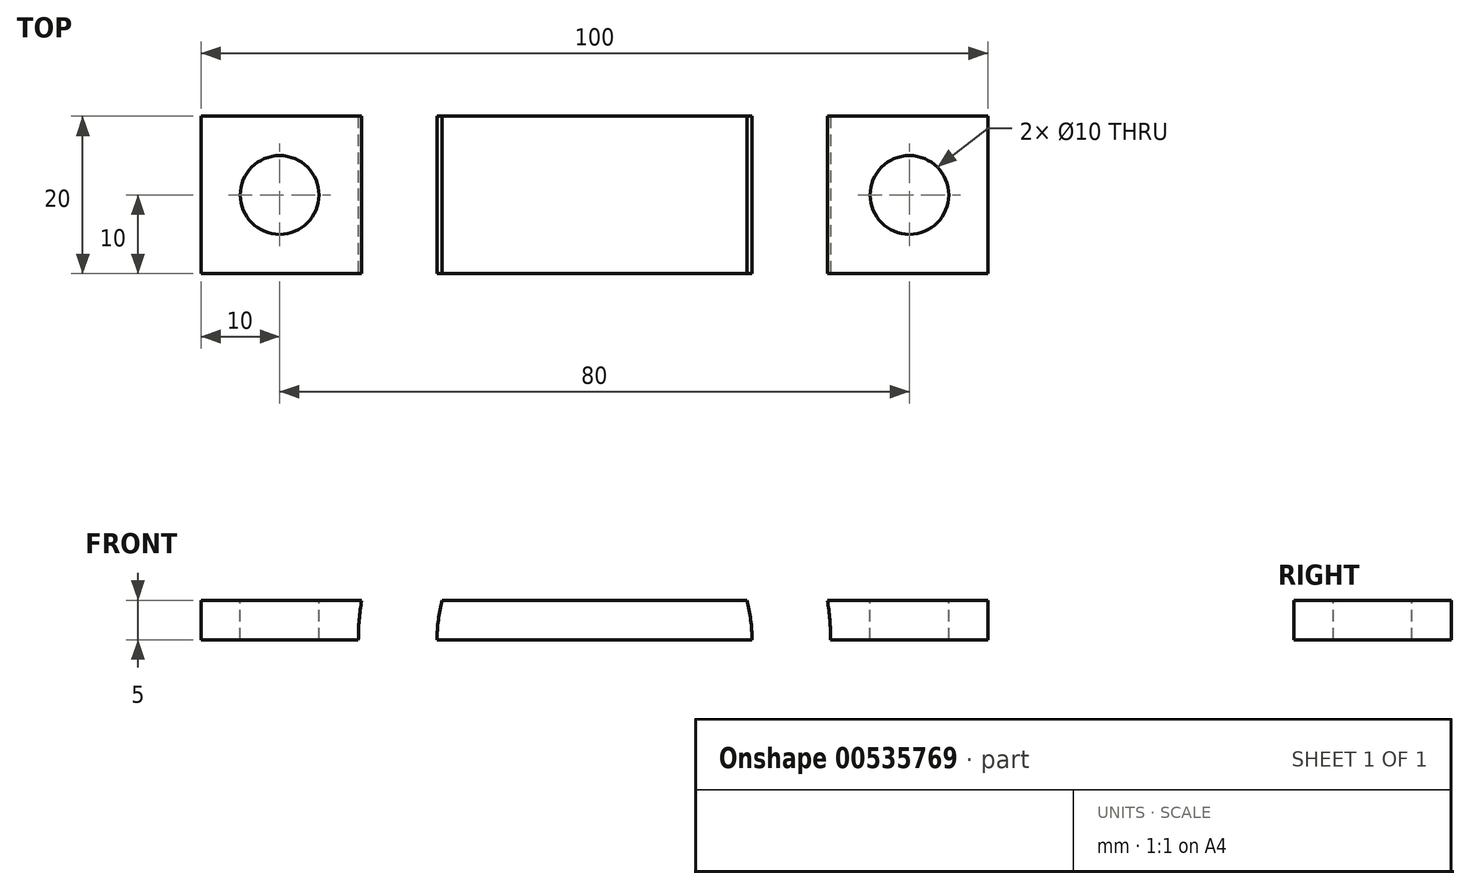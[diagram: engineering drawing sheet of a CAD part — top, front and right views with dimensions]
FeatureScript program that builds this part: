
annotation { "Feature Type Name" : "Feature", "Feature Type Description" : "" }
export const myFeature = defineFeature(function(context is Context, id is Id, definition is map)
    precondition{}
    {
        {
            var Q0;
            Q0=qCreatedBy(makeId("Front.planeOp"),FACE);
            var sketch = newSketch(context, id + "F0", { "sketchPlane" : qUnion([Q0])});
            skArc(sketch, "E0", {"start": v(-30, 0) * mm, "mid": v(-21.21, 21.21) * mm, "end": v(0, 30) * mm});
            skArc(sketch, "E1", {"start": v(-20, 0) * mm, "mid": v(-14.14, 14.14) * mm, "end": v(0, 20) * mm});
            skLineSegment(sketch, "E2", {"start": v(0, 30) * mm, "end": v(0, 0) * mm});
            skLineSegment(sketch, "E3", {"start": v(0, 0) * mm, "end": v(-30, 0) * mm});
            skSolve(sketch);
        }
        {
            var Q0;
            {var subQ0=sQuery(id+"F0.wireOp",EDGE,"E1");Q0=makeQuery(id+"F0.imprint","IMPRINT",FACE,{"disambiguationData":[TD([[makeQuery(id+"F0.imprint","IMPRINT",EDGE,{"derivedFrom":subQ0}),-1.0]])]});}
            var Q1;
            {var subQ0=sQuery(id+"F0.wireOp",EDGE,"E0");Q1=makeQuery(id+"F0.imprint","IMPRINT",FACE,{"disambiguationData":[TD([[makeQuery(id+"F0.imprint","IMPRINT",EDGE,{"derivedFrom":subQ0}),-1.0]])]});}
            extrude(context, id + "F1", {"entities" : qUnion([Q0, Q1]), "oppositeDirection" : true, "depth" : 60 * mm, "offsetDistance" : 25 * mm});
        }
        {
            var Q0;
            Q0=makeQuery(id+"F1.opExtrude","SWEPT_FACE",FACE,{"disambiguationData":[OSD([sQuery(id+"F0.wireOp",EDGE,"E2")])]});
            var sketch = newSketch(context, id + "F2", { "sketchPlane" : qUnion([Q0])});
            skLineSegment(sketch, "E4", {"start": v(60, 0) * mm, "end": v(40, 0) * mm});
            skLineSegment(sketch, "E5", {"start": v(40, 0) * mm, "end": v(40, 5) * mm});
            skLineSegment(sketch, "E6", {"start": v(40, 5) * mm, "end": v(60, 5) * mm});
            skLineSegment(sketch, "E7", {"start": v(60, 5) * mm, "end": v(60, 0) * mm});
            skSolve(sketch);
        }
        {
            var Q0;
            Q0=makeQuery(id+"F2.imprint","IMPRINT",FACE,{"disambiguationData":[TD([[makeQuery(id+"F2.imprint","IMPRINT",EDGE,{"derivedFrom":sQuery(id+"F2.wireOp",EDGE,"E4")}),-1.0]])]});
            extrude(context, id + "F3", {"entities" : qUnion([Q0]), "operationType" : NewBodyOperationType.ADD, "oppositeDirection" : true, "depth" : 50 * mm, "offsetDistance" : 25 * mm});
        }
        {
            var Q0;
            Q0=makeQuery(id+"F3.opExtrude","SWEPT_FACE",FACE,{"disambiguationData":[OSD([sQuery(id+"F2.wireOp",EDGE,"E6")])]});
            var sketch = newSketch(context, id + "F4", { "sketchPlane" : qUnion([Q0])});
            skLineSegment(sketch, "E8", {"start": v(-50, 60) * mm, "end": v(-50, 50) * mm});
            skLineSegment(sketch, "E9", {"start": v(-50, 50) * mm, "end": v(-40, 50) * mm});
            skLineSegment(sketch, "E10", {"start": v(-40, 50) * mm, "end": v(0, 50) * mm});
            skCircle(sketch, "E11", {"center": v(-40, 50) * mm, "radius": 5 * mm});
            skLineSegment(sketch, "E12", {"start": v(-40, 50) * mm, "end": v(-40, 40) * mm});
            skLineSegment(sketch, "E13", {"start": v(-40, 40) * mm, "end": v(-29.58, 40) * mm});
            skLineSegment(sketch, "E14", {"start": v(-40, 50) * mm, "end": v(-40, 60) * mm});
            skLineSegment(sketch, "E15", {"start": v(-40, 60) * mm, "end": v(-29.58, 60) * mm});
            skArc(sketch, "E16", {"start": v(-40, 40) * mm, "mid": v(-50, 50) * mm, "end": v(-40, 60) * mm});
            skSolve(sketch);
        }
        {
            var Q0;
            {var subQ0=sQuery(id+"F0.wireOp",EDGE,"E1");Q0=makeQuery(id+"F0.imprint","IMPRINT",FACE,{"disambiguationData":[TD([[makeQuery(id+"F0.imprint","IMPRINT",EDGE,{"derivedFrom":subQ0}),-1.0]])]});}
            extrude(context, id + "F5", {"entities" : qUnion([Q0]), "operationType" : NewBodyOperationType.REMOVE, "endBound" : BoundingType.THROUGH_ALL, "oppositeDirection" : true, "depth" : 25 * mm, "offsetDistance" : 25 * mm});
        }
        {
            var Q0;
            Q0=qCreatedBy(makeId("Top.planeOp"),FACE);
            var sketch = newSketch(context, id + "F6", { "sketchPlane" : qUnion([Q0])});
            skLineSegment(sketch, "E17", {"start": v(0, 0) * mm, "end": v(-10, 0) * mm});
            skLineSegment(sketch, "E18", {"start": v(-10, 0) * mm, "end": v(-10, 20) * mm});
            skLineSegment(sketch, "E19", {"start": v(0, 0) * mm, "end": v(0, 20) * mm});
            skLineSegment(sketch, "E20", {"start": v(0, 20) * mm, "end": v(-10, 20) * mm});
            skArc(sketch, "E21", {"start": v(-10, 20) * mm, "mid": v(-7.07, 27.07) * mm, "end": v(0, 30) * mm});
            skLineSegment(sketch, "E22", {"start": v(0, 30) * mm, "end": v(0, 20) * mm});
            skSolve(sketch);
        }
        {
            var Q0;
            Q0 = qSketchRegion(id + "F6", true);
            extrude(context, id + "F7", {"entities" : qUnion([Q0]), "operationType" : NewBodyOperationType.REMOVE, "endBound" : BoundingType.THROUGH_ALL, "depth" : 25 * mm, "offsetDistance" : 25 * mm});
        }
        {
            var Q0;
            {var subQ1=sQuery(id+"F2.wireOp",EDGE,"E6");var subQ2=makeQuery(id+"F3.opExtrude","CAP_EDGE",EDGE,{"disambiguationData":[OSD([subQ1])],"isStart":false});var subQ4=makeQuery(id+"F3.opExtrude","SWEPT_EDGE",EDGE,{"disambiguationData":[OSD([sQuery(id+"F2.wireOp",EDGE,"E5"),subQ1])]});var subQ6=makeQuery(id+"F4.imprint","INTERSECT",VERTEX,{"derivedFrom":[subQ2,subQ4]});Q0=makeQuery(id+"F4.imprint","IMPRINT",FACE,{"disambiguationData":[TD([[makeQuery(id+"F4.imprint","IMPRINT",EDGE,{"disambiguationData":[TD([[subQ6,-1.0]])],"derivedFrom":subQ2}),-1.0]])]});}
            var Q1;
            {var subQ0=sQuery(id+"F4.wireOp",EDGE,"E8");Q1=makeQuery(id+"F4.imprint","IMPRINT",FACE,{"disambiguationData":[TD([[makeQuery(id+"F4.imprint","IMPRINT",EDGE,{"derivedFrom":subQ0}),-1.0]])]});}
            var Q2;
            {var subQ1=sQuery(id+"F4.wireOp",EDGE,"E9");var subQ3=sQuery(id+"F4.wireOp",EDGE,"E11");var subQ4=makeQuery(id+"F4.imprint","INTERSECT",VERTEX,{"derivedFrom":[subQ1,subQ3]});Q2=makeQuery(id+"F4.imprint","IMPRINT",FACE,{"disambiguationData":[TD([[makeQuery(id+"F4.imprint","IMPRINT",EDGE,{"disambiguationData":[TD([[subQ4,-1.0]])],"derivedFrom":subQ3}),1.0]])]});}
            var Q3;
            {var subQ1=sQuery(id+"F4.wireOp",EDGE,"E10");var subQ3=sQuery(id+"F4.wireOp",EDGE,"E11");var subQ4=makeQuery(id+"F4.imprint","INTERSECT",VERTEX,{"derivedFrom":[subQ1,subQ3]});Q3=makeQuery(id+"F4.imprint","IMPRINT",FACE,{"disambiguationData":[TD([[makeQuery(id+"F4.imprint","IMPRINT",EDGE,{"disambiguationData":[TD([[subQ4,1.0]])],"derivedFrom":subQ3}),1.0]])]});}
            var Q4;
            {var subQ1=sQuery(id+"F4.wireOp",EDGE,"E10");var subQ3=sQuery(id+"F4.wireOp",EDGE,"E11");var subQ4=makeQuery(id+"F4.imprint","INTERSECT",VERTEX,{"derivedFrom":[subQ1,subQ3]});Q4=makeQuery(id+"F4.imprint","IMPRINT",FACE,{"disambiguationData":[TD([[makeQuery(id+"F4.imprint","IMPRINT",EDGE,{"disambiguationData":[TD([[subQ4,-1.0]])],"derivedFrom":subQ3}),1.0]])]});}
            var Q5;
            {var subQ1=sQuery(id+"F4.wireOp",EDGE,"E9");var subQ3=sQuery(id+"F4.wireOp",EDGE,"E11");var subQ4=makeQuery(id+"F4.imprint","INTERSECT",VERTEX,{"derivedFrom":[subQ1,subQ3]});Q5=makeQuery(id+"F4.imprint","IMPRINT",FACE,{"disambiguationData":[TD([[makeQuery(id+"F4.imprint","IMPRINT",EDGE,{"disambiguationData":[TD([[subQ4,1.0]])],"derivedFrom":subQ3}),1.0]])]});}
            extrude(context, id + "F8", {"entities" : qUnion([Q0, Q1, Q2, Q3, Q4, Q5]), "operationType" : NewBodyOperationType.REMOVE, "endBound" : BoundingType.THROUGH_ALL, "oppositeDirection" : true, "depth" : 25 * mm, "offsetDistance" : 25 * mm});
        }
        {
            var Q0;
            Q0=makeQuery(id+"F1.opExtrude","SWEPT_BODY",BODY,{"disambiguationData":[OSD([sQuery(id+"F0.wireOp",EDGE,"E0"),sQuery(id+"F0.wireOp",EDGE,"E2"),sQuery(id+"F0.wireOp",EDGE,"E3")])]});
            var Q1;
            Q1=qCreatedBy(makeId("Right.planeOp"),FACE);
            mirror(context, id + "F9", {"operationType" : NewBodyOperationType.ADD, "entities" : qUnion([Q0]), "mirrorPlane" : qUnion([Q1])});
        }
    });
